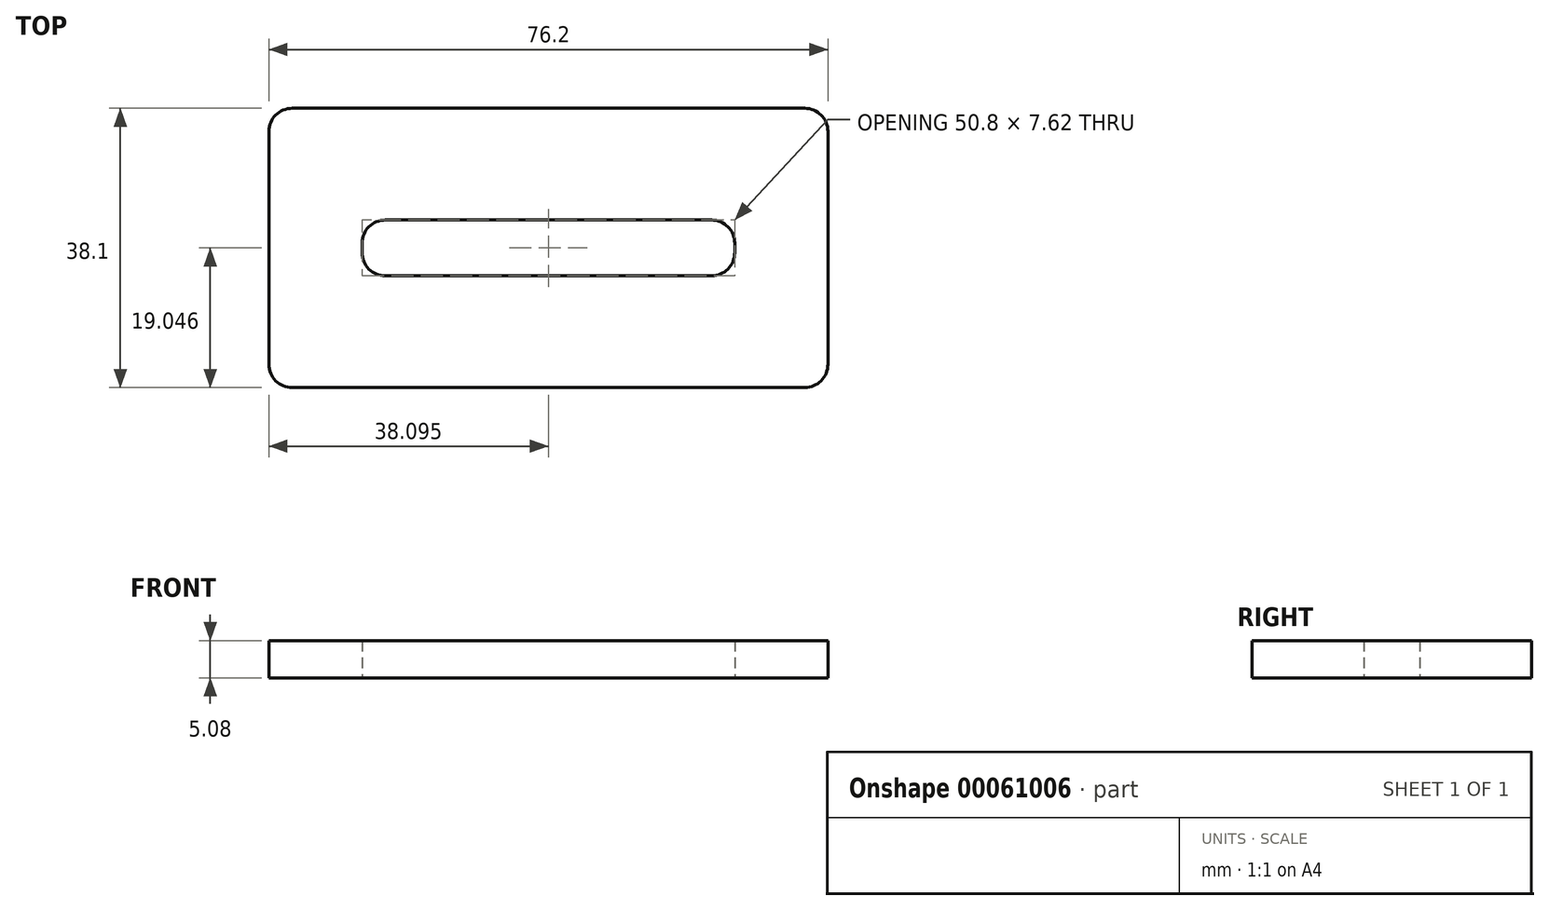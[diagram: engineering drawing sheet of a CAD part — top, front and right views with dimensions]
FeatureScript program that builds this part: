
annotation { "Feature Type Name" : "Feature", "Feature Type Description" : "" }
export const myFeature = defineFeature(function(context is Context, id is Id, definition is map)
    precondition{}
    {
        {
            var Q0;
            Q0=qCreatedBy(makeId("Top.planeOp"),FACE);
            var sketch = newSketch(context, id + "F0", { "sketchPlane" : qUnion([Q0])});
            skLineSegment(sketch, "E0.bottom", {"start": v(3.15, 38.22) * mm, "end": v(73, 38.22) * mm});
            skLineSegment(sketch, "E0.top", {"start": v(3.15, 0.12) * mm, "end": v(73, 0.12) * mm});
            skLineSegment(sketch, "E0.left", {"start": v(-0.02, 35.04) * mm, "end": v(-0.02, 3.3) * mm});
            skLineSegment(sketch, "E0.right", {"start": v(76.18, 35.04) * mm, "end": v(76.18, 3.3) * mm});
            skArc(sketch, "E1.filletArc", {"start": v(3.15, 38.22) * mm, "mid": v(0.9, 37.29) * mm, "end": v(-0.02, 35.04) * mm});
            skPoint(sketch, "E2.visualSharp", {"position": v(-0.02, 0.12) * mm});
            skArc(sketch, "E2.filletArc", {"start": v(-0.02, 3.3) * mm, "mid": v(0.9, 1.05) * mm, "end": v(3.15, 0.12) * mm});
            skPoint(sketch, "E3.visualSharp", {"position": v(76.18, 38.22) * mm});
            skArc(sketch, "E3.filletArc", {"start": v(76.18, 35.04) * mm, "mid": v(75.25, 37.29) * mm, "end": v(73, 38.22) * mm});
            skPoint(sketch, "E4.visualSharp", {"position": v(76.18, 0.12) * mm});
            skArc(sketch, "E4.filletArc", {"start": v(73, 0.12) * mm, "mid": v(75.25, 1.05) * mm, "end": v(76.18, 3.3) * mm});
            skLineSegment(sketch, "E5.bottom", {"start": v(15.85, 22.98) * mm, "end": v(60.3, 22.98) * mm});
            skLineSegment(sketch, "E5.top", {"start": v(15.85, 15.36) * mm, "end": v(60.3, 15.36) * mm});
            skLineSegment(sketch, "E5.left", {"start": v(12.68, 19.8) * mm, "end": v(12.68, 18.53) * mm});
            skLineSegment(sketch, "E5.right", {"start": v(63.48, 19.8) * mm, "end": v(63.48, 18.53) * mm});
            skPoint(sketch, "E6.visualSharp", {"position": v(12.68, 15.36) * mm});
            skArc(sketch, "E6.filletArc", {"start": v(12.68, 18.53) * mm, "mid": v(13.6, 16.29) * mm, "end": v(15.85, 15.36) * mm});
            skPoint(sketch, "E7.visualSharp", {"position": v(12.68, 22.98) * mm});
            skArc(sketch, "E7.filletArc", {"start": v(15.85, 22.98) * mm, "mid": v(13.6, 22.05) * mm, "end": v(12.68, 19.8) * mm});
            skPoint(sketch, "E8.visualSharp", {"position": v(63.48, 22.98) * mm});
            skArc(sketch, "E8.filletArc", {"start": v(63.48, 19.8) * mm, "mid": v(62.55, 22.05) * mm, "end": v(60.3, 22.98) * mm});
            skPoint(sketch, "E9.visualSharp", {"position": v(63.48, 15.36) * mm});
            skArc(sketch, "E9.filletArc", {"start": v(60.3, 15.36) * mm, "mid": v(62.55, 16.29) * mm, "end": v(63.48, 18.53) * mm});
            skSolve(sketch);
        }
        {
            var Q0;
            Q0 = qSketchRegion(id + "F0", true);
            extrude(context, id + "F1", {"entities" : qUnion([Q0]), "depth" : 5.08 * mm});
        }
    });
